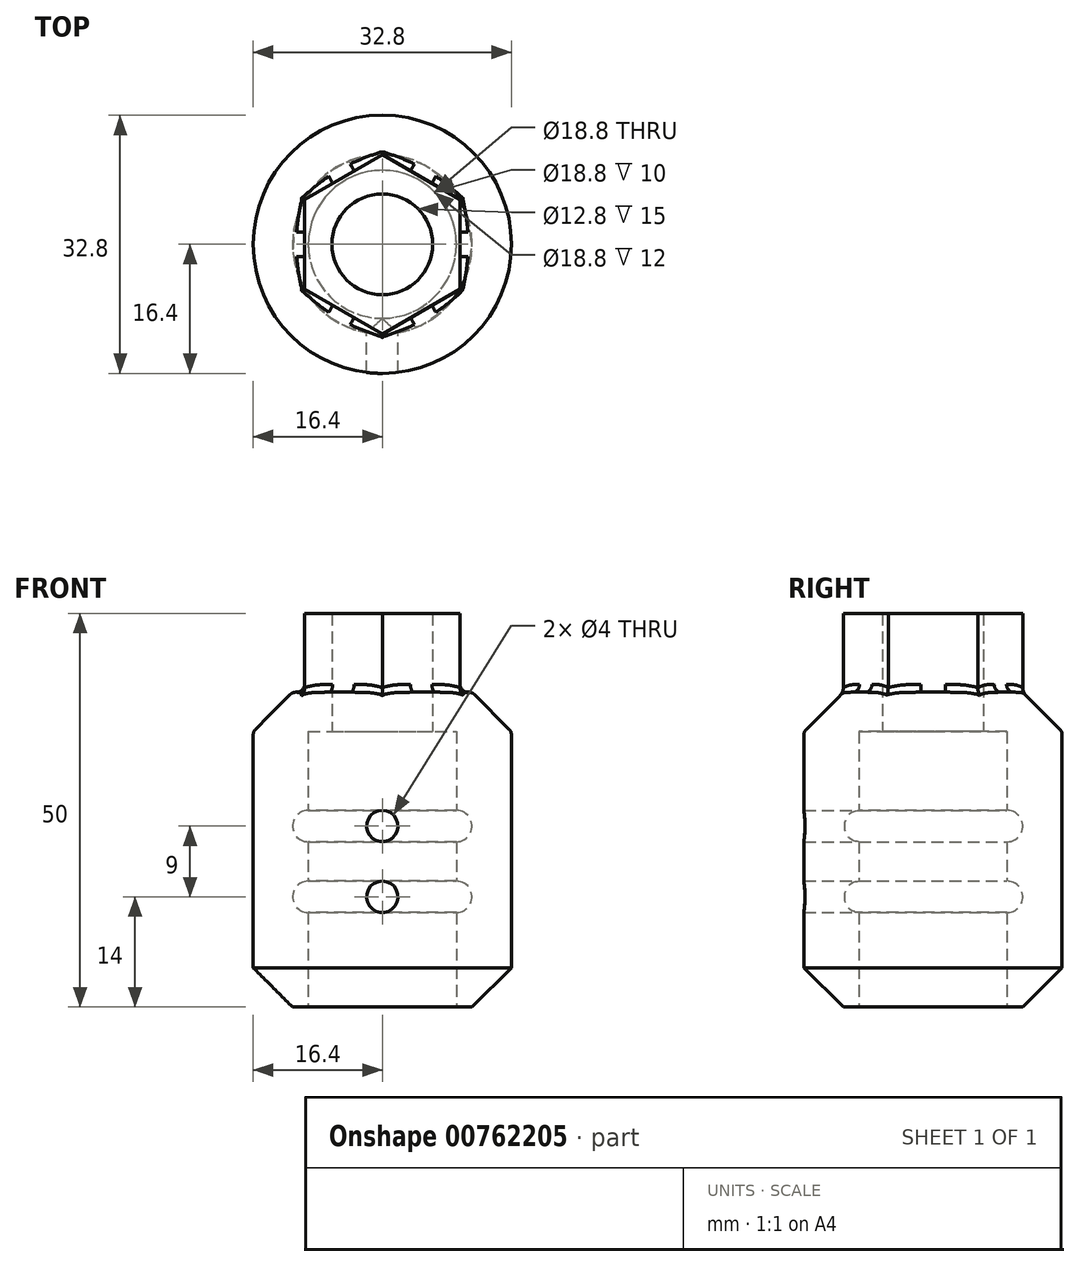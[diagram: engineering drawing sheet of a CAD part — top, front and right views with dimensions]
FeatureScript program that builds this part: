
annotation { "Feature Type Name" : "Feature", "Feature Type Description" : "" }
export const myFeature = defineFeature(function(context is Context, id is Id, definition is map)
    precondition{}
    {
        {
            var Q0;
            Q0=qCreatedBy(makeId("Right.planeOp"),FACE);
            var sketch = newSketch(context, id + "F0", { "sketchPlane" : qUnion([Q0])});
            skLineSegment(sketch, "E0", {"start": v(-16.4, 15) * mm, "end": v(-16.4, -15) * mm});
            skLineSegment(sketch, "E1", {"start": v(-11.4, -20) * mm, "end": v(-9.4, -20) * mm});
            skLineSegment(sketch, "E2", {"start": v(-6.4, 20) * mm, "end": v(-6.4, 15) * mm});
            skLineSegment(sketch, "E3", {"start": v(-6.4, 15) * mm, "end": v(-9.4, 15) * mm});
            skLineSegment(sketch, "E4", {"start": v(-9.4, 15) * mm, "end": v(-9.4, 5) * mm});
            skLineSegment(sketch, "E5", {"start": v(-9.4, 1) * mm, "end": v(-9.4, -4) * mm});
            skLineSegment(sketch, "E6", {"start": v(-9.4, -8) * mm, "end": v(-9.4, -20) * mm});
            skArc(sketch, "E7", {"start": v(-9.4, 5) * mm, "mid": v(-11.4, 3) * mm, "end": v(-9.4, 1) * mm});
            skArc(sketch, "E8", {"start": v(-9.4, -4) * mm, "mid": v(-11.4, -6) * mm, "end": v(-9.4, -8) * mm});
            skPoint(sketch, "E9.visualSharp", {"position": v(-16.4, 20) * mm});
            skPoint(sketch, "E10.visualSharp", {"position": v(-16.4, -20) * mm});
            skLineSegment(sketch, "E11", {"start": v(0, -22.5) * mm, "end": v(0, 23.87) * mm, "construction": true});
            skLineSegment(sketch, "E12", {"start": v(-16.4, 15) * mm, "end": v(-11.4, 20) * mm});
            skLineSegment(sketch, "E13", {"start": v(-16.4, -15) * mm, "end": v(-11.4, -20) * mm});
            skLineSegment(sketch, "E14", {"start": v(-11.4, 20) * mm, "end": v(-11.4, 30) * mm});
            skLineSegment(sketch, "E15", {"start": v(-11.4, 30) * mm, "end": v(-6.4, 30) * mm});
            skLineSegment(sketch, "E16", {"start": v(-6.4, 30) * mm, "end": v(-6.4, 20) * mm});
            skSolve(sketch);
        }
        {
            var Q0;
            Q0=makeQuery(id+"F0.imprint","IMPRINT",FACE,{"disambiguationData":[TD([[makeQuery(id+"F0.imprint","IMPRINT",EDGE,{"derivedFrom":sQuery(id+"F0.wireOp",EDGE,"E0")}),1.0]])]});
            var Q1;
            Q1=sQuery(id+"F0.wireOp",EDGE,"E11");
            revolve(context, id + "F1", {"surfaceOperationType" : NewSurfaceOperationType.NEW, "entities" : qUnion([Q0]), "axis" : qUnion([Q1]), "revolveType" : RevolveType.FULL});
        }
        {
            var Q0;
            Q0=qCreatedBy(makeId("Front.planeOp"),FACE);
            var sketch = newSketch(context, id + "F2", { "sketchPlane" : qUnion([Q0])});
            skCircle(sketch, "E17", {"center": v(0, 3) * mm, "radius": 2 * mm});
            skCircle(sketch, "E18", {"center": v(0, -6) * mm, "radius": 2 * mm});
            skSolve(sketch);
        }
        {
            var Q0;
            Q0 = qSketchRegion(id + "F2", true);
            extrude(context, id + "F3", {"entities" : qUnion([Q0]), "operationType" : NewBodyOperationType.REMOVE, "endBound" : BoundingType.THROUGH_ALL, "depth" : 25 * mm, "offsetDistance" : 25 * mm});
        }
        {
            var Q0;
            Q0=makeQuery(id+"F1.opRevolve","SWEPT_FACE",FACE,{"disambiguationData":[OSD([sQuery(id+"F0.wireOp",EDGE,"E15")])]});
            var sketch = newSketch(context, id + "F4", { "sketchPlane" : qUnion([Q0])});
            skCircle(sketch, "E19.cCircle", {"center": v(0, 0) * mm, "radius": 11.4 * mm, "construction": true});
            skLineSegment(sketch, "E19.0", {"start": v(0, 11.4) * mm, "end": v(9.87, 5.7) * mm});
            skLineSegment(sketch, "E19.1", {"start": v(9.87, 5.7) * mm, "end": v(9.87, -5.7) * mm});
            skLineSegment(sketch, "E19.2", {"start": v(9.87, -5.7) * mm, "end": v(0, -11.4) * mm});
            skLineSegment(sketch, "E19.3", {"start": v(0, -11.4) * mm, "end": v(-9.87, -5.7) * mm});
            skLineSegment(sketch, "E19.4", {"start": v(-9.87, -5.7) * mm, "end": v(-9.87, 5.7) * mm});
            skLineSegment(sketch, "E19.5", {"start": v(-9.87, 5.7) * mm, "end": v(0, 11.4) * mm});
            skCircle(sketch, "E20", {"center": v(0, 0) * mm, "radius": 11.4 * mm});
            skSolve(sketch);
        }
        {
            var Q0;
            {var subQ0=sQuery(id+"F4.wireOp",EDGE,"E19.0");Q0=makeQuery(id+"F4.imprint","IMPRINT",FACE,{"disambiguationData":[TD([[makeQuery(id+"F4.imprint","IMPRINT",EDGE,{"derivedFrom":subQ0}),1.0]])]});}
            var Q1;
            {var subQ0=sQuery(id+"F4.wireOp",EDGE,"E19.1");Q1=makeQuery(id+"F4.imprint","IMPRINT",FACE,{"disambiguationData":[TD([[makeQuery(id+"F4.imprint","IMPRINT",EDGE,{"derivedFrom":subQ0}),1.0]])]});}
            var Q2;
            {var subQ0=sQuery(id+"F4.wireOp",EDGE,"E19.5");Q2=makeQuery(id+"F4.imprint","IMPRINT",FACE,{"disambiguationData":[TD([[makeQuery(id+"F4.imprint","IMPRINT",EDGE,{"derivedFrom":subQ0}),1.0]])]});}
            var Q3;
            {var subQ0=sQuery(id+"F4.wireOp",EDGE,"E19.4");Q3=makeQuery(id+"F4.imprint","IMPRINT",FACE,{"disambiguationData":[TD([[makeQuery(id+"F4.imprint","IMPRINT",EDGE,{"derivedFrom":subQ0}),1.0]])]});}
            var Q4;
            {var subQ0=sQuery(id+"F4.wireOp",EDGE,"E19.2");Q4=makeQuery(id+"F4.imprint","IMPRINT",FACE,{"disambiguationData":[TD([[makeQuery(id+"F4.imprint","IMPRINT",EDGE,{"derivedFrom":subQ0}),1.0]])]});}
            var Q5;
            {var subQ0=sQuery(id+"F4.wireOp",EDGE,"E19.3");Q5=makeQuery(id+"F4.imprint","IMPRINT",FACE,{"disambiguationData":[TD([[makeQuery(id+"F4.imprint","IMPRINT",EDGE,{"derivedFrom":subQ0}),1.0]])]});}
            extrude(context, id + "F5", {"entities" : qUnion([Q0, Q1, Q2, Q3, Q4, Q5]), "operationType" : NewBodyOperationType.REMOVE, "oppositeDirection" : true, "depth" : 10 * mm, "offsetDistance" : 25 * mm});
        }
        {
            var Q0;
            {var subQ0=sQuery(id+"F4.wireOp",EDGE,"E20");var subQ1=sQuery(id+"F4.wireOp",EDGE,"E19.3");Q0=makeQuery(id+"F5.boolean.opBoolean","MERGE",EDGE,{"derivedFrom":[makeQuery(id+"F1.opRevolve","SWEPT_EDGE",EDGE,{"disambiguationData":[OSD([sQuery(id+"F0.wireOp",EDGE,"E12"),sQuery(id+"F0.wireOp",EDGE,"E14")])]}),makeQuery(id+"F5.opExtrude","CAP_EDGE",EDGE,{"disambiguationData":[OSD([subQ0]),TDD([makeQuery(id+"F4.imprint","IMPRINT",EDGE,{"disambiguationData":[TD([[makeQuery(id+"F4.imprint","INTERSECT",VERTEX,{"derivedFrom":[sQuery(id+"F4.wireOp",EDGE,"E19.2"),subQ1,subQ0]}),-1.0]])],"derivedFrom":subQ0})])],"isStart":false})]});}
            var Q1;
            {var subQ0=sQuery(id+"F4.wireOp",EDGE,"E20");var subQ1=sQuery(id+"F4.wireOp",EDGE,"E19.2");Q1=makeQuery(id+"F5.boolean.opBoolean","MERGE",EDGE,{"derivedFrom":[makeQuery(id+"F1.opRevolve","SWEPT_EDGE",EDGE,{"disambiguationData":[OSD([sQuery(id+"F0.wireOp",EDGE,"E12"),sQuery(id+"F0.wireOp",EDGE,"E14")])]}),makeQuery(id+"F5.opExtrude","CAP_EDGE",EDGE,{"disambiguationData":[OSD([subQ0]),TDD([makeQuery(id+"F4.imprint","IMPRINT",EDGE,{"disambiguationData":[TD([[makeQuery(id+"F4.imprint","INTERSECT",VERTEX,{"derivedFrom":[sQuery(id+"F4.wireOp",EDGE,"E19.1"),subQ1,subQ0]}),-1.0]])],"derivedFrom":subQ0})])],"isStart":false})]});}
            var Q2;
            {var subQ0=sQuery(id+"F4.wireOp",EDGE,"E20");var subQ1=sQuery(id+"F4.wireOp",EDGE,"E19.1");Q2=makeQuery(id+"F5.boolean.opBoolean","MERGE",EDGE,{"derivedFrom":[makeQuery(id+"F1.opRevolve","SWEPT_EDGE",EDGE,{"disambiguationData":[OSD([sQuery(id+"F0.wireOp",EDGE,"E12"),sQuery(id+"F0.wireOp",EDGE,"E14")])]}),makeQuery(id+"F5.opExtrude","CAP_EDGE",EDGE,{"disambiguationData":[OSD([subQ0]),TDD([makeQuery(id+"F4.imprint","IMPRINT",EDGE,{"disambiguationData":[TD([[makeQuery(id+"F4.imprint","INTERSECT",VERTEX,{"derivedFrom":[sQuery(id+"F4.wireOp",EDGE,"E19.0"),subQ1,subQ0]}),-1.0]])],"derivedFrom":subQ0})])],"isStart":false})]});}
            var Q3;
            Q3=makeQuery(id+"F1.opRevolve","SWEPT_FACE",FACE,{"disambiguationData":[OSD([sQuery(id+"F0.wireOp",EDGE,"E12")])]});
            fillet(context, id + "F6", {"entities" : qUnion([Q0, Q1, Q2, Q3]), "radius" : 1 * mm, "tangentPropagation" : true, "allowEdgeOverflow" : false});
        }
        {
            var Q0;
            {var subQ0=sQuery(id+"F4.wireOp",EDGE,"E20");var subQ1=sQuery(id+"F4.wireOp",EDGE,"E19.3");Q0=makeQuery(id+"F6.opFillet","BLEND_EDGE",EDGE,{"disambiguationData":[OD(0.0)],"blendedFrom":[makeQuery(id+"F5.boolean.opBoolean","MERGE",EDGE,{"derivedFrom":[makeQuery(id+"F1.opRevolve","SWEPT_EDGE",EDGE,{"disambiguationData":[OSD([sQuery(id+"F0.wireOp",EDGE,"E12"),sQuery(id+"F0.wireOp",EDGE,"E14")])]}),makeQuery(id+"F5.opExtrude","CAP_EDGE",EDGE,{"disambiguationData":[OSD([subQ0]),TDD([makeQuery(id+"F4.imprint","IMPRINT",EDGE,{"disambiguationData":[TD([[makeQuery(id+"F4.imprint","INTERSECT",VERTEX,{"derivedFrom":[sQuery(id+"F4.wireOp",EDGE,"E19.2"),subQ1,subQ0]}),-1.0]])],"derivedFrom":subQ0})])],"isStart":false})]}),makeQuery(id+"F5.boolean.opBoolean","COPY",FACE,{"derivedFrom":makeQuery(id+"F5.opExtrude","SWEPT_FACE",FACE,{"disambiguationData":[OSD([sQuery(id+"F4.wireOp",EDGE,"E19.0")])]})})],"blendedInto":[makeQuery(id+"F5.boolean.opBoolean","COPY",FACE,{"derivedFrom":makeQuery(id+"F5.opExtrude","SWEPT_FACE",FACE,{"disambiguationData":[OSD([sQuery(id+"F4.wireOp",EDGE,"E19.0")])]})})]});}
            var Q1;
            {var subQ0=sQuery(id+"F4.wireOp",EDGE,"E20");var subQ1=sQuery(id+"F4.wireOp",EDGE,"E19.3");Q1=makeQuery(id+"F6.opFillet","BLEND_EDGE",EDGE,{"disambiguationData":[OD(0.0)],"blendedFrom":[makeQuery(id+"F5.boolean.opBoolean","MERGE",EDGE,{"derivedFrom":[makeQuery(id+"F1.opRevolve","SWEPT_EDGE",EDGE,{"disambiguationData":[OSD([sQuery(id+"F0.wireOp",EDGE,"E12"),sQuery(id+"F0.wireOp",EDGE,"E14")])]}),makeQuery(id+"F5.opExtrude","CAP_EDGE",EDGE,{"disambiguationData":[OSD([subQ0]),TDD([makeQuery(id+"F4.imprint","IMPRINT",EDGE,{"disambiguationData":[TD([[makeQuery(id+"F4.imprint","INTERSECT",VERTEX,{"derivedFrom":[sQuery(id+"F4.wireOp",EDGE,"E19.2"),subQ1,subQ0]}),-1.0]])],"derivedFrom":subQ0})])],"isStart":false})]}),makeQuery(id+"F5.boolean.opBoolean","COPY",FACE,{"derivedFrom":makeQuery(id+"F5.opExtrude","SWEPT_FACE",FACE,{"disambiguationData":[OSD([sQuery(id+"F4.wireOp",EDGE,"E19.1")])]})})],"blendedInto":[makeQuery(id+"F5.boolean.opBoolean","COPY",FACE,{"derivedFrom":makeQuery(id+"F5.opExtrude","SWEPT_FACE",FACE,{"disambiguationData":[OSD([sQuery(id+"F4.wireOp",EDGE,"E19.1")])]})})]});}
            var Q2;
            Q2=makeQuery(id+"F5.boolean.opBoolean","COPY",EDGE,{"derivedFrom":makeQuery(id+"F5.opExtrude","CAP_EDGE",EDGE,{"disambiguationData":[OSD([sQuery(id+"F4.wireOp",EDGE,"E19.0")])],"isStart":false})});
            fillet(context, id + "F7", {"entities" : qUnion([Q0, Q1, Q2]), "radius" : 1 * mm, "tangentPropagation" : true, "allowEdgeOverflow" : false});
        }
        {
            var Q0;
            {var subQ0=sQuery(id+"F4.wireOp",EDGE,"E20");var subQ1=sQuery(id+"F4.wireOp",EDGE,"E19.3");Q0=makeQuery(id+"F6.opFillet","BLEND_EDGE",EDGE,{"disambiguationData":[OD(0.0)],"blendedFrom":[makeQuery(id+"F5.boolean.opBoolean","MERGE",EDGE,{"derivedFrom":[makeQuery(id+"F1.opRevolve","SWEPT_EDGE",EDGE,{"disambiguationData":[OSD([sQuery(id+"F0.wireOp",EDGE,"E12"),sQuery(id+"F0.wireOp",EDGE,"E14")])]}),makeQuery(id+"F5.opExtrude","CAP_EDGE",EDGE,{"disambiguationData":[OSD([subQ0]),TDD([makeQuery(id+"F4.imprint","IMPRINT",EDGE,{"disambiguationData":[TD([[makeQuery(id+"F4.imprint","INTERSECT",VERTEX,{"derivedFrom":[sQuery(id+"F4.wireOp",EDGE,"E19.2"),subQ1,subQ0]}),-1.0]])],"derivedFrom":subQ0})])],"isStart":false})]}),makeQuery(id+"F5.boolean.opBoolean","COPY",FACE,{"derivedFrom":makeQuery(id+"F5.opExtrude","SWEPT_FACE",FACE,{"disambiguationData":[OSD([sQuery(id+"F4.wireOp",EDGE,"E19.5")])]})})],"blendedInto":[makeQuery(id+"F5.boolean.opBoolean","COPY",FACE,{"derivedFrom":makeQuery(id+"F5.opExtrude","SWEPT_FACE",FACE,{"disambiguationData":[OSD([sQuery(id+"F4.wireOp",EDGE,"E19.5")])]})})]});}
            var Q1;
            Q1=makeQuery(id+"F5.boolean.opBoolean","COPY",EDGE,{"derivedFrom":makeQuery(id+"F5.opExtrude","CAP_EDGE",EDGE,{"disambiguationData":[OSD([sQuery(id+"F4.wireOp",EDGE,"E19.5")])],"isStart":false})});
            var Q2;
            {var subQ0=sQuery(id+"F4.wireOp",EDGE,"E19.4");var subQ1=sQuery(id+"F4.wireOp",EDGE,"E20");var subQ2=sQuery(id+"F4.wireOp",EDGE,"E19.3");Q2=makeQuery(id+"F6.opFillet","BLEND_EDGE",EDGE,{"disambiguationData":[OD(1.0)],"blendedFrom":[makeQuery(id+"F5.boolean.opBoolean","MERGE",EDGE,{"derivedFrom":[makeQuery(id+"F1.opRevolve","SWEPT_EDGE",EDGE,{"disambiguationData":[OSD([sQuery(id+"F0.wireOp",EDGE,"E12"),sQuery(id+"F0.wireOp",EDGE,"E14")])]}),makeQuery(id+"F5.opExtrude","CAP_EDGE",EDGE,{"disambiguationData":[OSD([subQ1]),TDD([makeQuery(id+"F4.imprint","IMPRINT",EDGE,{"disambiguationData":[TD([[makeQuery(id+"F4.imprint","INTERSECT",VERTEX,{"derivedFrom":[sQuery(id+"F4.wireOp",EDGE,"E19.2"),subQ2,subQ1]}),-1.0]])],"derivedFrom":subQ1})])],"isStart":false})]}),makeQuery(id+"F5.boolean.opBoolean","COPY",FACE,{"derivedFrom":makeQuery(id+"F5.opExtrude","SWEPT_FACE",FACE,{"disambiguationData":[OSD([subQ0])]})})],"blendedInto":[makeQuery(id+"F5.boolean.opBoolean","COPY",FACE,{"derivedFrom":makeQuery(id+"F5.opExtrude","SWEPT_FACE",FACE,{"disambiguationData":[OSD([subQ0])]})})]});}
            var Q3;
            {var subQ0=sQuery(id+"F4.wireOp",EDGE,"E19.3");var subQ1=sQuery(id+"F4.wireOp",EDGE,"E20");Q3=makeQuery(id+"F6.opFillet","BLEND_EDGE",EDGE,{"disambiguationData":[OD(1.0)],"blendedFrom":[makeQuery(id+"F5.boolean.opBoolean","MERGE",EDGE,{"derivedFrom":[makeQuery(id+"F1.opRevolve","SWEPT_EDGE",EDGE,{"disambiguationData":[OSD([sQuery(id+"F0.wireOp",EDGE,"E12"),sQuery(id+"F0.wireOp",EDGE,"E14")])]}),makeQuery(id+"F5.opExtrude","CAP_EDGE",EDGE,{"disambiguationData":[OSD([subQ1]),TDD([makeQuery(id+"F4.imprint","IMPRINT",EDGE,{"disambiguationData":[TD([[makeQuery(id+"F4.imprint","INTERSECT",VERTEX,{"derivedFrom":[sQuery(id+"F4.wireOp",EDGE,"E19.2"),subQ0,subQ1]}),-1.0]])],"derivedFrom":subQ1})])],"isStart":false})]}),makeQuery(id+"F5.boolean.opBoolean","COPY",FACE,{"derivedFrom":makeQuery(id+"F5.opExtrude","SWEPT_FACE",FACE,{"disambiguationData":[OSD([subQ0])]})})],"blendedInto":[makeQuery(id+"F5.boolean.opBoolean","COPY",FACE,{"derivedFrom":makeQuery(id+"F5.opExtrude","SWEPT_FACE",FACE,{"disambiguationData":[OSD([subQ0])]})})]});}
            var Q4;
            {var subQ0=sQuery(id+"F4.wireOp",EDGE,"E19.2");var subQ1=sQuery(id+"F4.wireOp",EDGE,"E20");var subQ2=sQuery(id+"F4.wireOp",EDGE,"E19.3");Q4=makeQuery(id+"F6.opFillet","BLEND_EDGE",EDGE,{"disambiguationData":[OD(1.0)],"blendedFrom":[makeQuery(id+"F5.boolean.opBoolean","MERGE",EDGE,{"derivedFrom":[makeQuery(id+"F1.opRevolve","SWEPT_EDGE",EDGE,{"disambiguationData":[OSD([sQuery(id+"F0.wireOp",EDGE,"E12"),sQuery(id+"F0.wireOp",EDGE,"E14")])]}),makeQuery(id+"F5.opExtrude","CAP_EDGE",EDGE,{"disambiguationData":[OSD([subQ1]),TDD([makeQuery(id+"F4.imprint","IMPRINT",EDGE,{"disambiguationData":[TD([[makeQuery(id+"F4.imprint","INTERSECT",VERTEX,{"derivedFrom":[subQ0,subQ2,subQ1]}),-1.0]])],"derivedFrom":subQ1})])],"isStart":false})]}),makeQuery(id+"F5.boolean.opBoolean","COPY",FACE,{"derivedFrom":makeQuery(id+"F5.opExtrude","SWEPT_FACE",FACE,{"disambiguationData":[OSD([subQ0])]})})],"blendedInto":[makeQuery(id+"F5.boolean.opBoolean","COPY",FACE,{"derivedFrom":makeQuery(id+"F5.opExtrude","SWEPT_FACE",FACE,{"disambiguationData":[OSD([subQ0])]})})]});}
            var Q5;
            {var subQ0=sQuery(id+"F4.wireOp",EDGE,"E19.2");var subQ1=sQuery(id+"F4.wireOp",EDGE,"E20");var subQ2=sQuery(id+"F4.wireOp",EDGE,"E19.3");Q5=makeQuery(id+"F6.opFillet","BLEND_EDGE",EDGE,{"disambiguationData":[OD(0.0)],"blendedFrom":[makeQuery(id+"F5.boolean.opBoolean","MERGE",EDGE,{"derivedFrom":[makeQuery(id+"F1.opRevolve","SWEPT_EDGE",EDGE,{"disambiguationData":[OSD([sQuery(id+"F0.wireOp",EDGE,"E12"),sQuery(id+"F0.wireOp",EDGE,"E14")])]}),makeQuery(id+"F5.opExtrude","CAP_EDGE",EDGE,{"disambiguationData":[OSD([subQ1]),TDD([makeQuery(id+"F4.imprint","IMPRINT",EDGE,{"disambiguationData":[TD([[makeQuery(id+"F4.imprint","INTERSECT",VERTEX,{"derivedFrom":[subQ0,subQ2,subQ1]}),-1.0]])],"derivedFrom":subQ1})])],"isStart":false})]}),makeQuery(id+"F5.boolean.opBoolean","COPY",FACE,{"derivedFrom":makeQuery(id+"F5.opExtrude","SWEPT_FACE",FACE,{"disambiguationData":[OSD([subQ0])]})})],"blendedInto":[makeQuery(id+"F5.boolean.opBoolean","COPY",FACE,{"derivedFrom":makeQuery(id+"F5.opExtrude","SWEPT_FACE",FACE,{"disambiguationData":[OSD([subQ0])]})})]});}
            fillet(context, id + "F8", {"entities" : qUnion([Q0, Q1, Q2, Q3, Q4, Q5]), "radius" : 1 * mm, "tangentPropagation" : true, "allowEdgeOverflow" : false});
        }
    });
